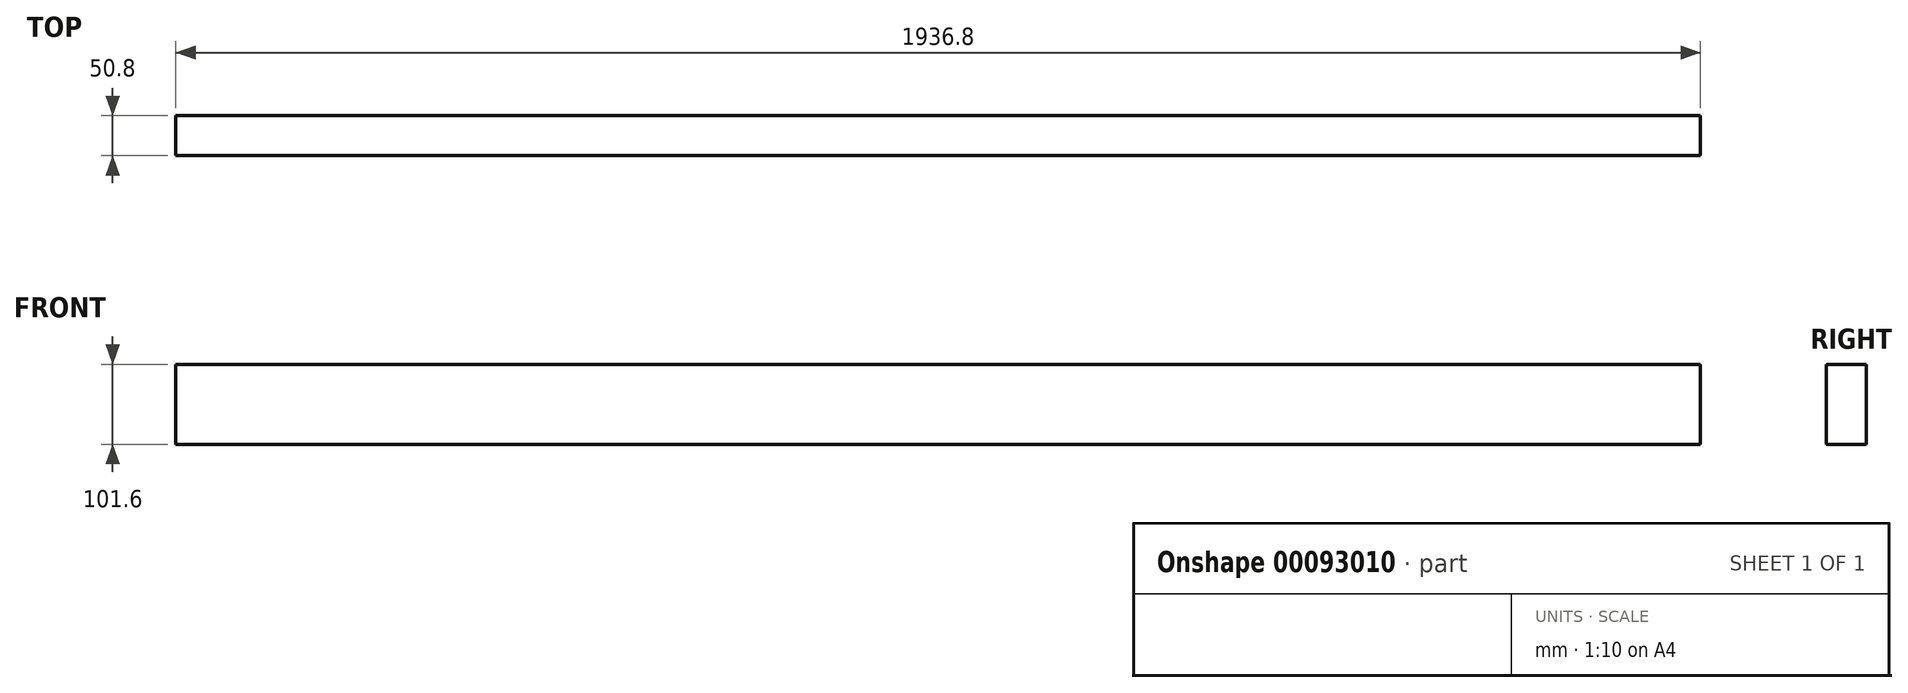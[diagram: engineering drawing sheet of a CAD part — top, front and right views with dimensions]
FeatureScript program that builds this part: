
annotation { "Feature Type Name" : "Feature", "Feature Type Description" : "" }
export const myFeature = defineFeature(function(context is Context, id is Id, definition is map)
    precondition{}
    {
        {
            var Q0;
            Q0=qCreatedBy(makeId("Right.planeOp"),FACE);
            var sketch = newSketch(context, id + "F0", { "sketchPlane" : qUnion([Q0])});
            skLineSegment(sketch, "E0.bottom", {"start": v(-25.4, -50.8) * mm, "end": v(25.4, -50.8) * mm});
            skLineSegment(sketch, "E0.top", {"start": v(-25.4, 50.8) * mm, "end": v(25.4, 50.8) * mm});
            skLineSegment(sketch, "E0.left", {"start": v(-25.4, -50.8) * mm, "end": v(-25.4, 50.8) * mm});
            skLineSegment(sketch, "E0.right", {"start": v(25.4, -50.8) * mm, "end": v(25.4, 50.8) * mm});
            skPoint(sketch, "E0.middle", {"position": v(0, 0) * mm});
            skSolve(sketch);
        }
        {
            var Q0;
            Q0=makeQuery(id+"F0.imprint","IMPRINT",FACE,{"disambiguationData":[TD([[makeQuery(id+"F0.imprint","IMPRINT",EDGE,{"derivedFrom":sQuery(id+"F0.wireOp",EDGE,"E0.bottom")}),1.0]])]});
            extrude(context, id + "F1", {"entities" : qUnion([Q0]), "endBound" : BoundingType.SYMMETRIC, "depth" : 1936.8 * mm});
        }
    });
